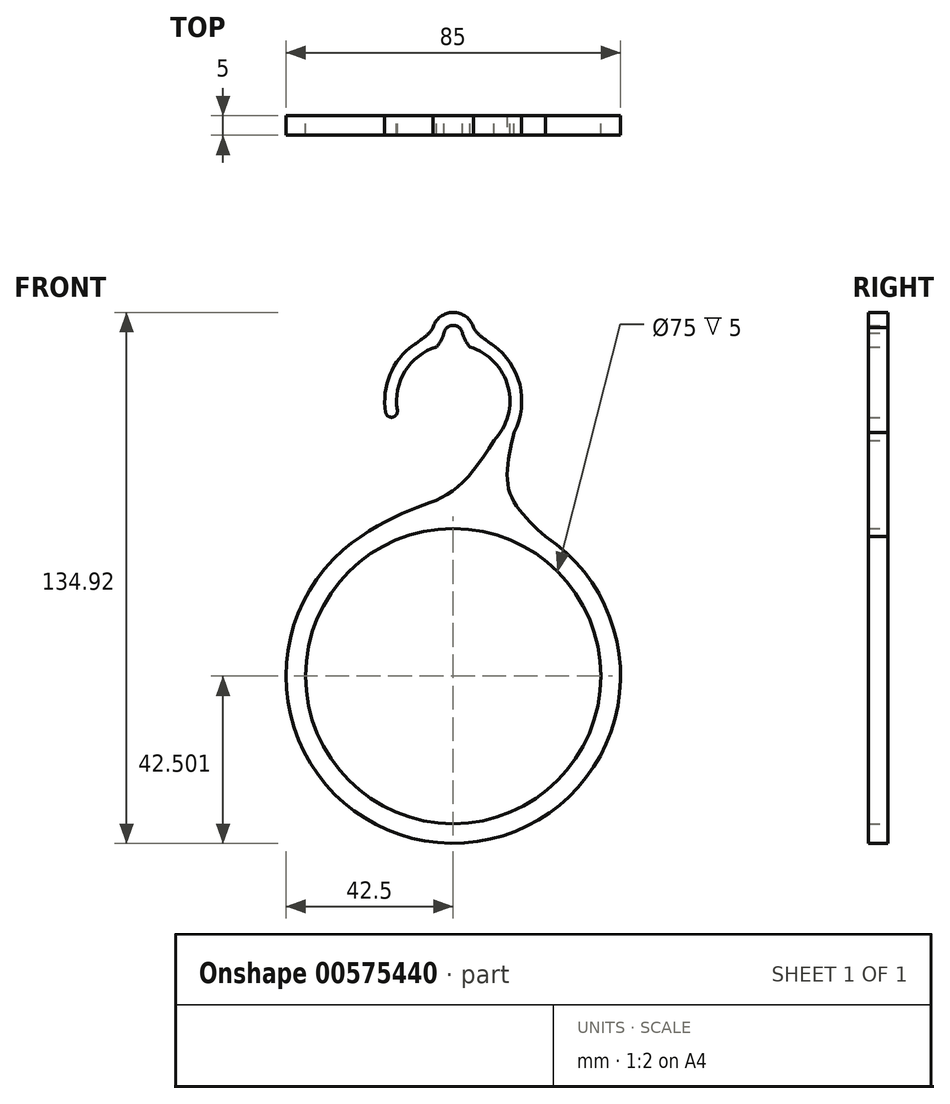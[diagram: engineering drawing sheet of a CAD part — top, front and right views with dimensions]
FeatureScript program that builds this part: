
annotation { "Feature Type Name" : "Feature", "Feature Type Description" : "" }
export const myFeature = defineFeature(function(context is Context, id is Id, definition is map)
    precondition{}
    {
        {
            var Q0;
            Q0=qCreatedBy(makeId("Front.planeOp"),FACE);
            var sketch = newSketch(context, id + "F0", { "sketchPlane" : qUnion([Q0])});
            skArc(sketch, "E0.0", {"start": v(5.2, 18.57) * mm, "mid": v(0, 22.49) * mm, "end": v(-5.2, 18.57) * mm});
            skArc(sketch, "E1", {"start": v(10.33, -10.06) * mm, "mid": v(13.95, 3.55) * mm, "end": v(4.23, 13.73) * mm});
            skArc(sketch, "E2", {"start": v(2.36, 17.21) * mm, "mid": v(-0.06, 19.17) * mm, "end": v(-2.38, 17.1) * mm});
            skArc(sketch, "E3", {"start": v(2.36, 17.21) * mm, "mid": v(3.06, 15.35) * mm, "end": v(4.23, 13.73) * mm});
            skArc(sketch, "E4.converted", {"start": v(15.47, -8) * mm, "mid": v(16.9, 4.1) * mm, "end": v(10.06, 14.17) * mm});
            skLineSegment(sketch, "E5.MirrorCS", {"start": v(-15.29, -4.13) * mm, "end": v(-15.29, -4.13) * mm});
            skPoint(sketch, "E6", {"position": v(-13.9, -3.76) * mm});
            skPoint(sketch, "E7", {"position": v(0.03, -14.43) * mm});
            skFitSpline(sketch, "E8", {"points": [v(5.2, 18.57) * mm, v(6.06, 17.32) * mm, v(10.06, 14.17) * mm], "startDerivative": vector(1.79, -3.38) * mm, "endDerivative": vector(7.41, -5.26) * mm});
            skFitSpline(sketch, "E9.MirrorCS", {"points": [v(-5.2, 18.57) * mm, v(-6.06, 17.32) * mm, v(-10.06, 14.17) * mm], "startDerivative": vector(-1.79, -3.38) * mm, "endDerivative": vector(-7.41, -5.26) * mm});
            skArc(sketch, "E10.MirrorCS", {"start": v(-2.36, 17.21) * mm, "mid": v(-3.06, 15.35) * mm, "end": v(-4.23, 13.73) * mm});
            skArc(sketch, "E11.trimOffspring", {"start": v(-4.23, 13.73) * mm, "mid": v(-12.26, 7.53) * mm, "end": v(-14.2, -2.43) * mm});
            skArc(sketch, "E12.trimOffspring", {"start": v(-2.36, 17.21) * mm, "mid": v(-2.36, 17.21) * mm, "end": v(-2.36, 17.2) * mm});
            skArc(sketch, "E13.trimOffspring", {"start": v(-10.06, 14.17) * mm, "mid": v(-16.07, 6.64) * mm, "end": v(-17.16, -2.93) * mm});
            skCircle(sketch, "E14", {"center": v(0, -69.93) * mm, "radius": 37.5 * mm});
            skCircle(sketch, "E15.0", {"center": v(0, -69.93) * mm, "radius": 42.5 * mm});
            skFitSpline(sketch, "E16", {"points": [v(15.47, -8) * mm, v(14.27, -22.97) * mm, v(23.5, -34.51) * mm], "startDerivative": vector(-7.6, -31.55) * mm, "endDerivative": vector(23.69, -21.55) * mm});
            skFitSpline(sketch, "E17", {"points": [v(10.33, -10.06) * mm, v(0.04, -22.76) * mm, v(-9.3, -27.14) * mm, v(-27.94, -37.9) * mm], "startDerivative": vector(-29.25, -47.4) * mm, "endDerivative": vector(-49.05, -42.8) * mm});
            skPoint(sketch, "E18.visualSharp", {"position": v(-16.8, -4.53) * mm});
            skArc(sketch, "E18.filletArc", {"start": v(-17.16, -2.93) * mm, "mid": v(-16.49, -3.94) * mm, "end": v(-15.29, -4.13) * mm});
            skArc(sketch, "E19.filletArc", {"start": v(-15.29, -4.13) * mm, "mid": v(-14.42, -3.49) * mm, "end": v(-14.2, -2.43) * mm});
            skPoint(sketch, "E20.end.orphan", {"position": v(0.04, -17.43) * mm});
            skSolve(sketch);
        }
        {
            var Q0;
            Q0 = qSketchRegion(id + "F0", true);
            extrude(context, id + "F1", {"entities" : qUnion([Q0]), "endBound" : BoundingType.SYMMETRIC, "depth" : 5 * mm, "offsetDistance" : 25 * mm});
        }
    });
